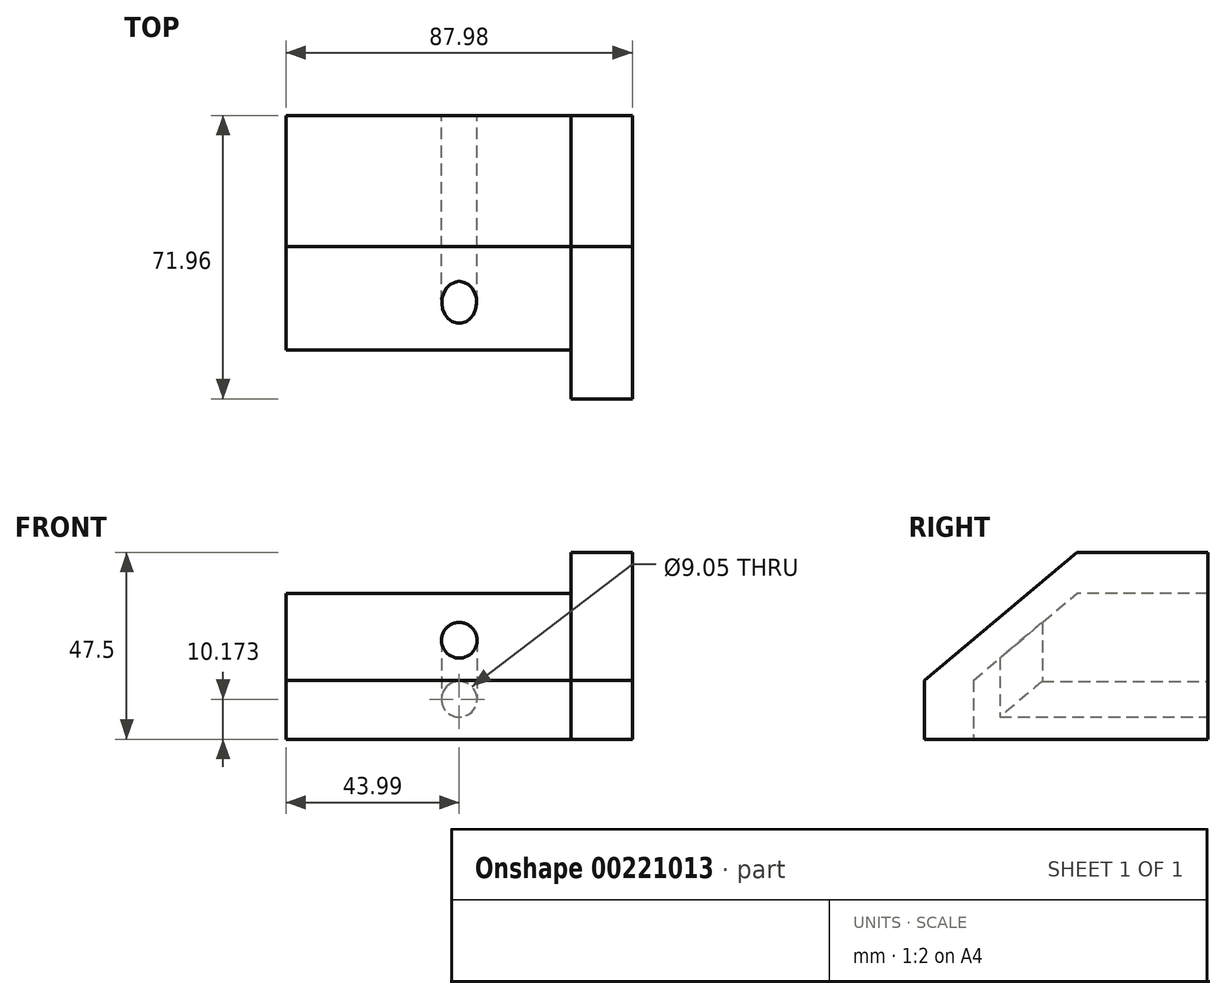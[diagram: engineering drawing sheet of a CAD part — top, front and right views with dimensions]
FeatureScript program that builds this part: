
annotation { "Feature Type Name" : "Feature", "Feature Type Description" : "" }
export const myFeature = defineFeature(function(context is Context, id is Id, definition is map)
    precondition{}
    {
        {
            var Q0;
            Q0=qCreatedBy(makeId("Top.planeOp"),FACE);
            var sketch = newSketch(context, id + "F0", { "sketchPlane" : qUnion([Q0])});
            skLineSegment(sketch, "E0.bottom", {"start": v(-44, 45.18) * mm, "end": v(44, 45.18) * mm});
            skLineSegment(sketch, "E0.top", {"start": v(-44, -45.18) * mm, "end": v(44, -45.18) * mm});
            skLineSegment(sketch, "E0.left", {"start": v(-44, 45.18) * mm, "end": v(-44, -45.18) * mm});
            skLineSegment(sketch, "E0.right", {"start": v(44, 45.18) * mm, "end": v(44, -45.18) * mm});
            skPoint(sketch, "E0.middle", {"position": v(0, 0) * mm});
            skLineSegment(sketch, "E1", {"start": v(28.41, 45.18) * mm, "end": v(28.41, -45.18) * mm});
            skLineSegment(sketch, "E2", {"start": v(28.41, -45.18) * mm, "end": v(28.41, 45.18) * mm});
            skSolve(sketch);
        }
        {
            var Q0;
            {var subQ0=sQuery(id+"F0.wireOp",EDGE,"E0.right");Q0=makeQuery(id+"F0.imprint","IMPRINT",FACE,{"disambiguationData":[TD([[makeQuery(id+"F0.imprint","IMPRINT",EDGE,{"derivedFrom":subQ0}),-1.0]])]});}
            var sketch = newSketch(context, id + "F1", { "sketchPlane" : qUnion([Q0])});
            skSolve(sketch);
        }
        {
            var Q0;
            {var subQ0=sQuery(id+"F0.wireOp",EDGE,"E0.left");Q0=makeQuery(id+"F0.imprint","IMPRINT",FACE,{"disambiguationData":[TD([[makeQuery(id+"F0.imprint","IMPRINT",EDGE,{"derivedFrom":subQ0}),1.0]])]});}
            extrude(context, id + "F2", {"entities" : qUnion([Q0]), "depth" : 22.1 * mm});
        }
        {
            var Q0;
            Q0 = qSketchRegion(id + "F1", true);
            var Q1;
            {var subQ0=sQuery(id+"F0.wireOp",EDGE,"E0.right");Q1=makeQuery(id+"F1.imprint","IMPRINT",FACE,{"disambiguationData":[TD([[makeQuery(id+"F1.imprint","IMPRINT",EDGE,{"derivedFrom":makeQuery(id+"F0.imprint","IMPRINT",EDGE,{"derivedFrom":subQ0})}),-1.0]])]});}
            extrude(context, id + "F3", {"entities" : qUnion([Q0, Q1]), "operationType" : NewBodyOperationType.ADD, "depth" : 32.5 * mm});
        }
        {
            var Q0;
            Q0=makeQuery(id+"F2.opExtrude","CAP_EDGE",EDGE,{"disambiguationData":[OSD([sQuery(id+"F0.wireOp",EDGE,"E0.top")])],"isStart":false});
            chamfer(context, id + "F4", {"entities" : qUnion([Q0]), "chamferType" : ChamferType.OFFSET_ANGLE, "width" : 57.15 * mm, "oppositeDirection" : false, "angle" : 40 * degree, "tangentPropagation" : true});
        }
        {
            var Q0;
            Q0=makeQuery(id+"F3.opExtrude","CAP_EDGE",EDGE,{"disambiguationData":[OSD([sQuery(id+"F0.wireOp",EDGE,"E0.top")])],"isStart":false});
            chamfer(context, id + "F5", {"entities" : qUnion([Q0]), "chamferType" : ChamferType.OFFSET_ANGLE, "width" : 57.15 * mm, "oppositeDirection" : false, "angle" : 40 * degree, "tangentPropagation" : true});
        }
        {
            var Q0;
            {var subQ0=sQuery(id+"F0.wireOp",EDGE,"E0.bottom");Q0=makeQuery(id+"F3.boolean.opBoolean","MERGE",FACE,{"derivedFrom":[makeQuery(id+"F2.opExtrude","SWEPT_FACE",FACE,{"disambiguationData":[OSD([subQ0])]}),makeQuery(id+"F3.opExtrude","SWEPT_FACE",FACE,{"disambiguationData":[OSD([subQ0])]})]});}
            var sketch = newSketch(context, id + "F6", { "sketchPlane" : qUnion([Q0])});
            skCircle(sketch, "E3", {"center": v(0, 10.17) * mm, "radius": 4.53 * mm});
            skSolve(sketch);
        }
        {
            var Q0;
            Q0=makeQuery(id+"F6.imprint","IMPRINT",FACE,{"disambiguationData":[TD([[makeQuery(id+"F6.imprint","IMPRINT",EDGE,{"derivedFrom":sQuery(id+"F6.wireOp",EDGE,"E3")}),1.0]])]});
            extrude(context, id + "F7", {"entities" : qUnion([Q0]), "operationType" : NewBodyOperationType.REMOVE, "endBound" : BoundingType.THROUGH_ALL, "oppositeDirection" : true, "depth" : 25.4 * mm});
        }
        {
            var Q0;
            Q0=makeQuery(id+"F2.opExtrude","CAP_FACE",FACE,{"disambiguationData":[OSD([sQuery(id+"F0.wireOp",EDGE,"E0.bottom"),sQuery(id+"F0.wireOp",EDGE,"E0.top"),sQuery(id+"F0.wireOp",EDGE,"E0.left"),sQuery(id+"F0.wireOp",EDGE,"E2")])],"isStart":false});
            var Q1;
            Q1=makeQuery(id+"F4.opChamfer","BLEND_FACE",FACE,{"disambiguationData":[OSD([sQuery(id+"F0.wireOp",EDGE,"E0.top")])]});
            var Q2;
            Q2=makeQuery(id+"F5.opChamfer","BLEND_FACE",FACE,{"disambiguationData":[OSD([sQuery(id+"F0.wireOp",EDGE,"E0.top")])]});
            var Q3;
            Q3=makeQuery(id+"F3.opExtrude","CAP_FACE",FACE,{"disambiguationData":[OSD([sQuery(id+"F0.wireOp",EDGE,"E0.bottom"),sQuery(id+"F0.wireOp",EDGE,"E0.top"),sQuery(id+"F0.wireOp",EDGE,"E0.right"),sQuery(id+"F0.wireOp",EDGE,"E2")])],"isStart":false});
            extrude(context, id + "F8", {"entities" : qUnion([Q0, Q1, Q2, Q3]), "operationType" : NewBodyOperationType.ADD, "depth" : 15 * mm});
        }
    });
